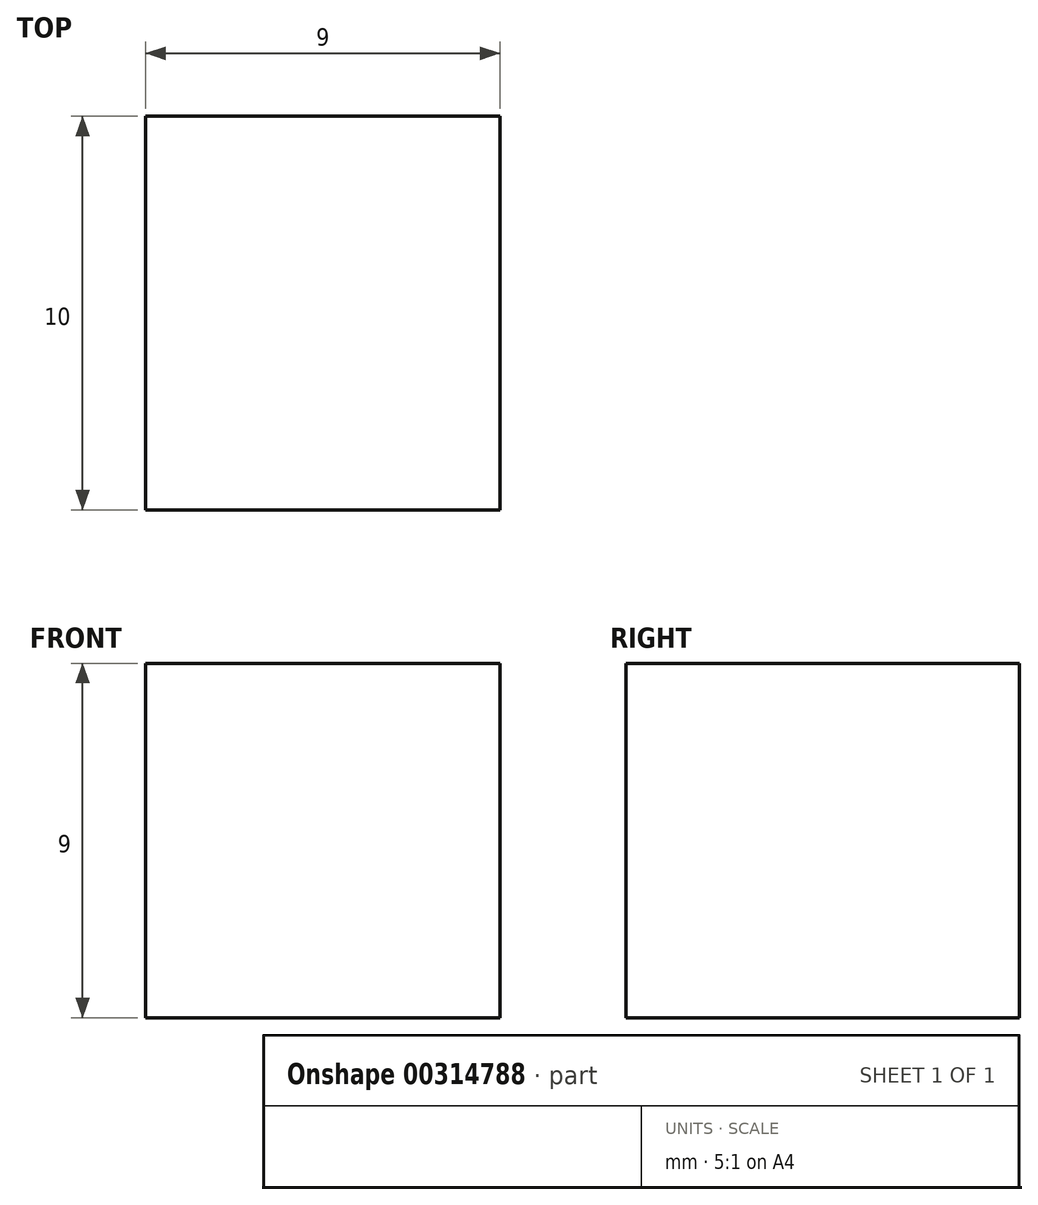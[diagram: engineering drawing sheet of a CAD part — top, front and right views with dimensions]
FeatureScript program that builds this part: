
annotation { "Feature Type Name" : "Feature", "Feature Type Description" : "" }
export const myFeature = defineFeature(function(context is Context, id is Id, definition is map)
    precondition{}
    {
        {
            var Q0;
            Q0=qCreatedBy(makeId("Front.planeOp"),FACE);
            var sketch = newSketch(context, id + "F0", { "sketchPlane" : qUnion([Q0])});
            skLineSegment(sketch, "E0.bottom", {"start": v(0, 0) * mm, "end": v(45, 0) * mm});
            skLineSegment(sketch, "E0.top", {"start": v(0, 40) * mm, "end": v(45, 40) * mm});
            skLineSegment(sketch, "E0.left", {"start": v(0, 0) * mm, "end": v(0, 40) * mm});
            skLineSegment(sketch, "E0.right", {"start": v(45, 0) * mm, "end": v(45, 40) * mm});
            skLineSegment(sketch, "E1.bottom", {"start": v(15, 0) * mm, "end": v(30, 0) * mm});
            skLineSegment(sketch, "E1.top", {"start": v(15, 5) * mm, "end": v(30, 5) * mm});
            skLineSegment(sketch, "E1.left", {"start": v(15, 0) * mm, "end": v(15, 5) * mm});
            skLineSegment(sketch, "E1.right", {"start": v(30, 0) * mm, "end": v(30, 5) * mm});
            skLineSegment(sketch, "E2.bottom", {"start": v(0, 40) * mm, "end": v(9, 40) * mm});
            skLineSegment(sketch, "E2.top", {"start": v(0, 10) * mm, "end": v(9, 10) * mm});
            skLineSegment(sketch, "E2.left", {"start": v(0, 40) * mm, "end": v(0, 10) * mm});
            skLineSegment(sketch, "E2.right", {"start": v(9, 40) * mm, "end": v(9, 10) * mm});
            skLineSegment(sketch, "E3.bottom", {"start": v(45, 40) * mm, "end": v(36, 40) * mm});
            skLineSegment(sketch, "E3.top", {"start": v(45, 10) * mm, "end": v(36, 10) * mm});
            skLineSegment(sketch, "E3.left", {"start": v(45, 40) * mm, "end": v(45, 10) * mm});
            skLineSegment(sketch, "E3.right", {"start": v(36, 40) * mm, "end": v(36, 10) * mm});
            skLineSegment(sketch, "E4.bottom", {"start": v(18, 40) * mm, "end": v(27, 40) * mm});
            skLineSegment(sketch, "E4.top", {"start": v(18, 31) * mm, "end": v(27, 31) * mm});
            skLineSegment(sketch, "E4.left", {"start": v(18, 40) * mm, "end": v(18, 31) * mm});
            skLineSegment(sketch, "E4.right", {"start": v(27, 40) * mm, "end": v(27, 31) * mm});
            skSolve(sketch);
        }
        {
            var Q0;
            Q0=makeQuery(id+"F0.imprint","IMPRINT",FACE,{"disambiguationData":[TD([[makeQuery(id+"F0.imprint","IMPRINT",EDGE,{"derivedFrom":sQuery(id+"F0.wireOp",EDGE,"E4.top")}),1.0]])]});
            var Q1;
            Q1=makeQuery(id+"F0.imprint","IMPRINT",FACE,{"disambiguationData":[TD([[makeQuery(id+"F0.imprint","IMPRINT",EDGE,{"derivedFrom":sQuery(id+"F0.wireOp",EDGE,"E1.top")}),1.0]])]});
            extrude(context, id + "F1", {"entities" : qUnion([Q0, Q1]), "oppositeDirection" : true, "depth" : 40 * mm});
        }
        {
            var Q0;
            Q0=makeQuery(id+"F0.imprint","IMPRINT",FACE,{"disambiguationData":[TD([[makeQuery(id+"F0.imprint","IMPRINT",EDGE,{"derivedFrom":sQuery(id+"F0.wireOp",EDGE,"E4.top")}),1.0]])]});
            extrude(context, id + "F2", {"entities" : qUnion([Q0]), "operationType" : NewBodyOperationType.REMOVE, "oppositeDirection" : true, "depth" : 30 * mm});
        }
    });
